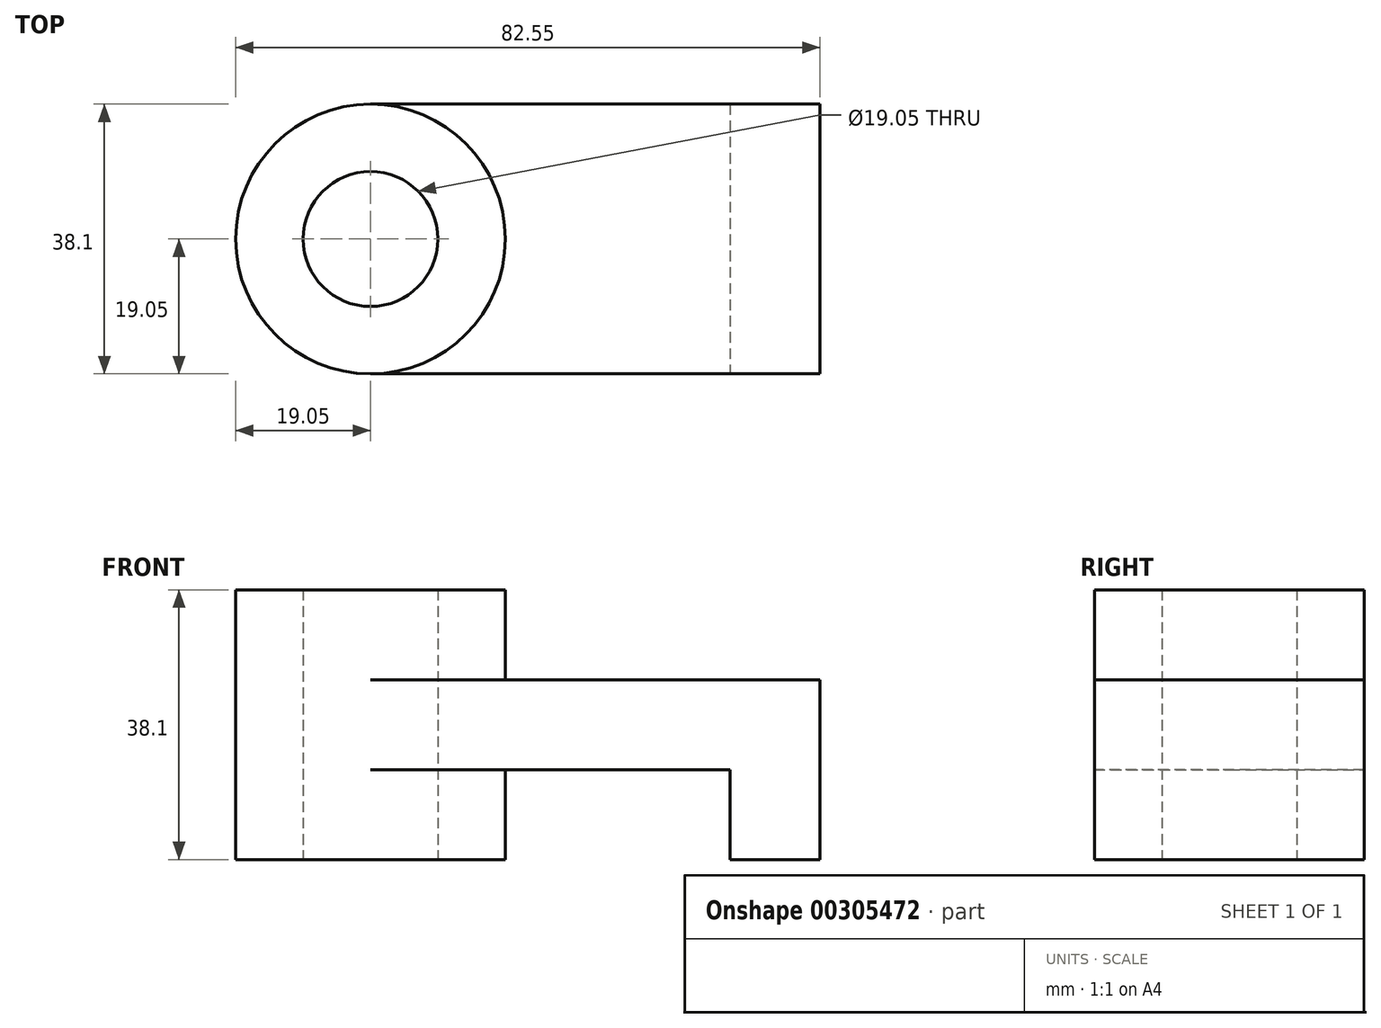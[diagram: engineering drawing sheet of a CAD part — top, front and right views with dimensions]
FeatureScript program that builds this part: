
annotation { "Feature Type Name" : "Feature", "Feature Type Description" : "" }
export const myFeature = defineFeature(function(context is Context, id is Id, definition is map)
    precondition{}
    {
        {
            var Q0;
            Q0=qCreatedBy(makeId("Top.planeOp"),FACE);
            var sketch = newSketch(context, id + "F0", { "sketchPlane" : qUnion([Q0])});
            skLineSegment(sketch, "E0.bottom", {"start": v(-25.4, 19.05) * mm, "end": v(25.4, 19.05) * mm});
            skLineSegment(sketch, "E0.top", {"start": v(-25.4, -19.05) * mm, "end": v(25.4, -19.05) * mm});
            skLineSegment(sketch, "E0.right", {"start": v(25.4, 19.05) * mm, "end": v(25.4, -19.05) * mm});
            skPoint(sketch, "E0.middle", {"position": v(0, 0) * mm});
            skCircle(sketch, "E1", {"center": v(-25.4, 0) * mm, "radius": 19.05 * mm});
            skCircle(sketch, "E2", {"center": v(-25.4, 0) * mm, "radius": 9.53 * mm});
            skSolve(sketch);
        }
        {
            var Q0;
            Q0=makeQuery(id+"F0.imprint","IMPRINT",FACE,{"disambiguationData":[TD([[makeQuery(id+"F0.imprint","IMPRINT",EDGE,{"derivedFrom":sQuery(id+"F0.wireOp",EDGE,"E2")}),-1.0]])]});
            var Q1;
            {var subQ0=sQuery(id+"F0.wireOp",EDGE,"E0.bottom");Q1=makeQuery(id+"F0.imprint","IMPRINT",FACE,{"disambiguationData":[TD([[makeQuery(id+"F0.imprint","IMPRINT",EDGE,{"derivedFrom":subQ0}),-1.0]])]});}
            extrude(context, id + "F1", {"entities" : qUnion([Q0, Q1]), "endBound" : BoundingType.SYMMETRIC, "depth" : 12.7 * mm});
        }
        {
            var Q0;
            Q0=qCreatedBy(makeId("Top.planeOp"),FACE);
            var sketch = newSketch(context, id + "F2", { "sketchPlane" : qUnion([Q0])});
            skCircle(sketch, "E3", {"center": v(-25.4, 0) * mm, "radius": 19.05 * mm});
            skCircle(sketch, "E4", {"center": v(-25.4, 0) * mm, "radius": 9.53 * mm});
            skSolve(sketch);
        }
        {
            var Q0;
            Q0 = qSketchRegion(id + "F2", true);
            extrude(context, id + "F3", {"entities" : qUnion([Q0]), "operationType" : NewBodyOperationType.ADD, "endBound" : BoundingType.SYMMETRIC, "depth" : 38.1 * mm});
        }
        {
            var Q0;
            Q0=makeQuery(id+"F1.opExtrude","CAP_FACE",FACE,{"disambiguationData":[OSD([sQuery(id+"F0.wireOp",EDGE,"E0.bottom"),sQuery(id+"F0.wireOp",EDGE,"E0.top"),sQuery(id+"F0.wireOp",EDGE,"E0.right"),sQuery(id+"F0.wireOp",EDGE,"E1"),sQuery(id+"F0.wireOp",EDGE,"E2")])],"isStart":false});
            var sketch = newSketch(context, id + "F4", { "sketchPlane" : qUnion([Q0])});
            skLineSegment(sketch, "E5.bottom", {"start": v(25.4, 19.05) * mm, "end": v(38.1, 19.05) * mm});
            skLineSegment(sketch, "E5.top", {"start": v(25.4, -19.05) * mm, "end": v(38.1, -19.05) * mm});
            skLineSegment(sketch, "E5.left", {"start": v(25.4, 19.05) * mm, "end": v(25.4, -19.05) * mm});
            skLineSegment(sketch, "E5.right", {"start": v(38.1, 19.05) * mm, "end": v(38.1, -19.05) * mm});
            skSolve(sketch);
        }
        {
            var Q0;
            Q0 = qSketchRegion(id + "F4", true);
            extrude(context, id + "F5", {"entities" : qUnion([Q0]), "operationType" : NewBodyOperationType.ADD, "oppositeDirection" : true, "depth" : 25.4 * mm});
        }
    });
